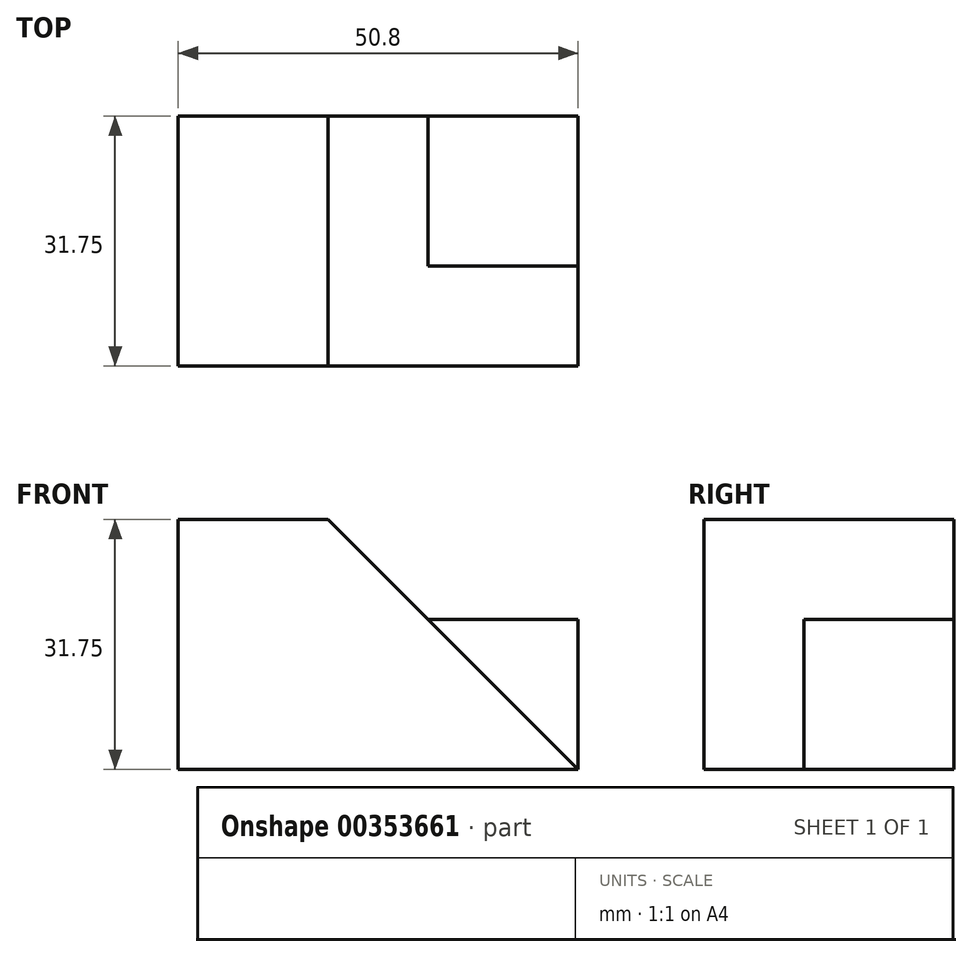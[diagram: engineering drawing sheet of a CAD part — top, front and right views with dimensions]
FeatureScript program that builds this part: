
annotation { "Feature Type Name" : "Feature", "Feature Type Description" : "" }
export const myFeature = defineFeature(function(context is Context, id is Id, definition is map)
    precondition{}
    {
        {
            var Q0;
            Q0=qCreatedBy(makeId("Front.planeOp"),FACE);
            var sketch = newSketch(context, id + "F0", { "sketchPlane" : qUnion([Q0])});
            skLineSegment(sketch, "E0", {"start": v(-50.8, 31.75) * mm, "end": v(-50.8, 0) * mm});
            skLineSegment(sketch, "E1", {"start": v(-50.8, 0) * mm, "end": v(0, 0) * mm});
            skLineSegment(sketch, "E2", {"start": v(0, 0) * mm, "end": v(0, 31.75) * mm});
            skLineSegment(sketch, "E3", {"start": v(0, 31.75) * mm, "end": v(-50.8, 31.75) * mm});
            skSolve(sketch);
        }
        {
            var Q0;
            Q0=makeQuery(id+"F0.imprint","IMPRINT",FACE,{"disambiguationData":[TD([[makeQuery(id+"F0.imprint","IMPRINT",EDGE,{"derivedFrom":sQuery(id+"F0.wireOp",EDGE,"E0")}),1.0]])]});
            extrude(context, id + "F1", {"entities" : qUnion([Q0]), "depth" : 31.75 * mm});
        }
        {
            var Q0;
            Q0=makeQuery(id+"F1.opExtrude","CAP_FACE",FACE,{"disambiguationData":[OSD([sQuery(id+"F0.wireOp",EDGE,"E0"),sQuery(id+"F0.wireOp",EDGE,"E1"),sQuery(id+"F0.wireOp",EDGE,"E2"),sQuery(id+"F0.wireOp",EDGE,"E3")])],"isStart":false});
            var sketch = newSketch(context, id + "F2", { "sketchPlane" : qUnion([Q0])});
            skLineSegment(sketch, "E4", {"start": v(-31.75, 31.75) * mm, "end": v(0, 0) * mm});
            skSolve(sketch);
        }
        {
            var Q0;
            {var subQ0=sQuery(id+"F2.wireOp",EDGE,"E4");Q0=makeQuery(id+"F2.imprint","IMPRINT",FACE,{"disambiguationData":[TD([[makeQuery(id+"F2.imprint","IMPRINT",EDGE,{"derivedFrom":subQ0}),1.0]])]});}
            extrude(context, id + "F3", {"entities" : qUnion([Q0]), "operationType" : NewBodyOperationType.REMOVE, "oppositeDirection" : true, "depth" : 12.7 * mm});
        }
        {
            var Q0;
            Q0=makeQuery(id+"F3.boolean.opBoolean","COPY",FACE,{"derivedFrom":makeQuery(id+"F3.opExtrude","CAP_FACE",FACE,{"disambiguationData":[OSD([sQuery(id+"F0.wireOp",EDGE,"E2"),sQuery(id+"F0.wireOp",EDGE,"E3"),sQuery(id+"F2.wireOp",EDGE,"E4")])],"isStart":false})});
            var sketch = newSketch(context, id + "F4", { "sketchPlane" : qUnion([Q0])});
            skLineSegment(sketch, "E5", {"start": v(-19.05, 19.05) * mm, "end": v(0, 19.05) * mm});
            skSolve(sketch);
        }
        {
            var Q0;
            {var subQ0=sQuery(id+"F4.wireOp",EDGE,"E5");Q0=makeQuery(id+"F4.imprint","IMPRINT",FACE,{"disambiguationData":[TD([[makeQuery(id+"F4.imprint","IMPRINT",EDGE,{"derivedFrom":subQ0}),1.0]])]});}
            extrude(context, id + "F5", {"entities" : qUnion([Q0]), "operationType" : NewBodyOperationType.REMOVE, "oppositeDirection" : true, "depth" : 19.05 * mm});
        }
    });
